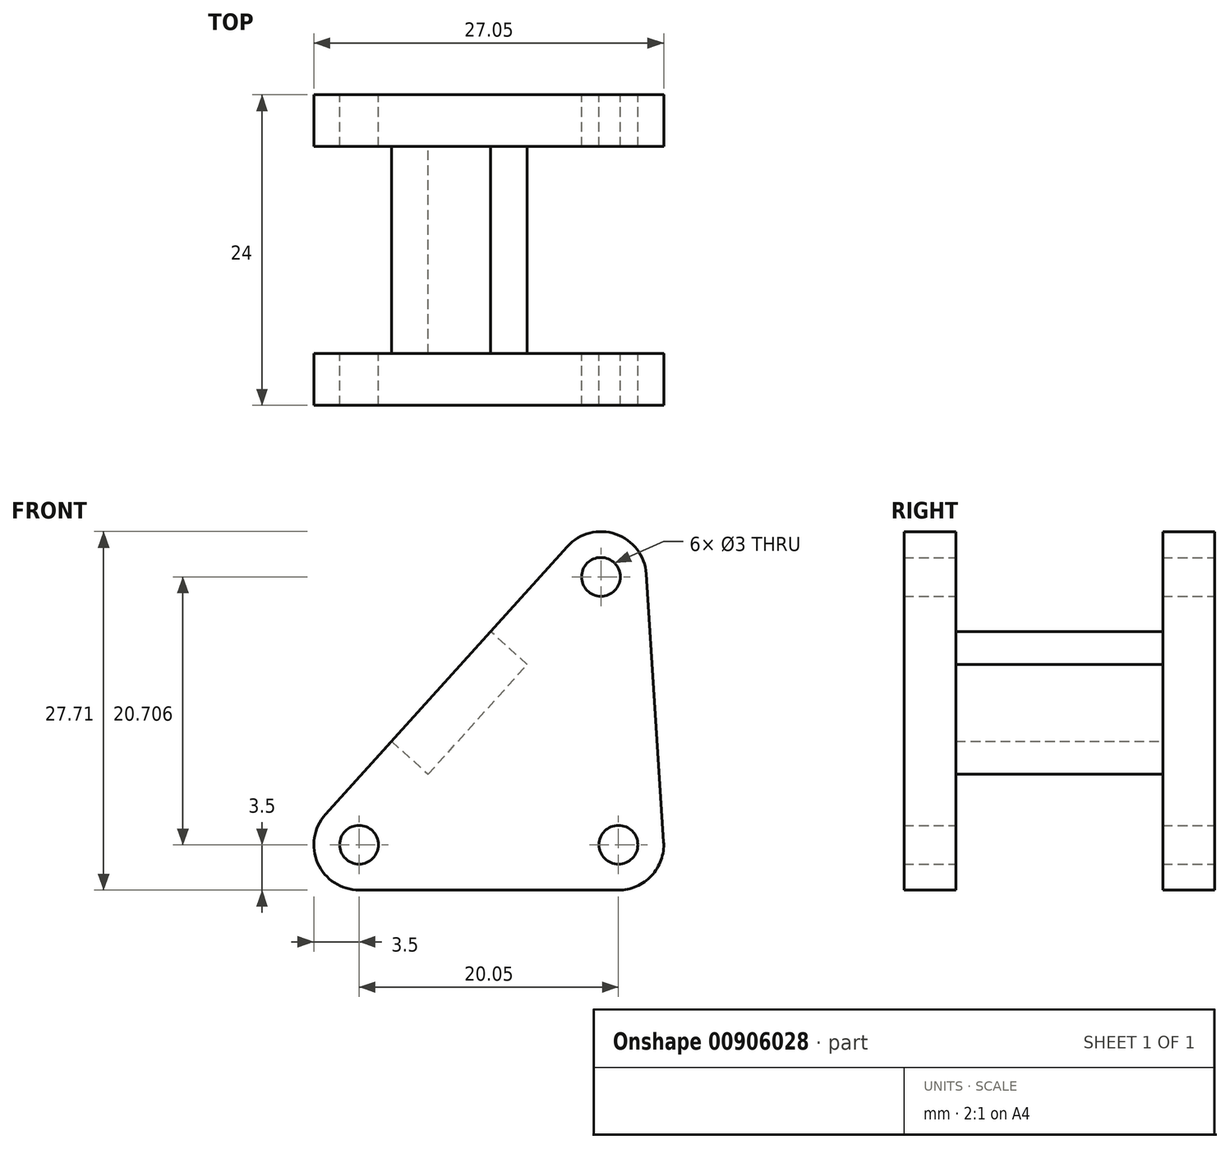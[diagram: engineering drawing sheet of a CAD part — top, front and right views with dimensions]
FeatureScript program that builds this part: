
annotation { "Feature Type Name" : "Feature", "Feature Type Description" : "" }
export const myFeature = defineFeature(function(context is Context, id is Id, definition is map)
    precondition{}
    {
        {
            var Q0;
            Q0=qCreatedBy(makeId("Front.planeOp"),FACE);
            var sketch = newSketch(context, id + "F0", { "sketchPlane" : qUnion([Q0])});
            skCircle(sketch, "E0", {"center": v(0, 0) * mm, "radius": 1.5 * mm});
            skCircle(sketch, "E1", {"center": v(20.05, 0) * mm, "radius": 1.5 * mm});
            skCircle(sketch, "E2", {"center": v(18.7, 20.7) * mm, "radius": 1.5 * mm});
            skLineSegment(sketch, "E3", {"start": v(-2.6, 2.35) * mm, "end": v(16.1, 23.05) * mm});
            skLineSegment(sketch, "E4", {"start": v(22.2, 20.93) * mm, "end": v(23.54, 0.23) * mm});
            skLineSegment(sketch, "E5", {"start": v(20.05, -3.5) * mm, "end": v(0, -3.5) * mm});
            skPoint(sketch, "E6.visualSharp", {"position": v(-7.88, -3.5) * mm});
            skArc(sketch, "E6.filletArc", {"start": v(-2.6, 2.35) * mm, "mid": v(-3.2, -1.42) * mm, "end": v(0, -3.5) * mm});
            skPoint(sketch, "E7.visualSharp", {"position": v(23.79, -3.5) * mm});
            skArc(sketch, "E7.filletArc", {"start": v(20.05, -3.5) * mm, "mid": v(22.6, -2.4) * mm, "end": v(23.54, 0.23) * mm});
            skPoint(sketch, "E8.visualSharp", {"position": v(21.65, 29.2) * mm});
            skArc(sketch, "E8.filletArc", {"start": v(22.2, 20.93) * mm, "mid": v(19.85, 24.01) * mm, "end": v(16.1, 23.05) * mm});
            skSolve(sketch);
        }
        {
            var Q0;
            Q0=qSketchRegion(id+"F0",true);
            extrude(context, id + "F1", {"entities" : qUnion([Q0]), "endBound" : BoundingType.SYMMETRIC, "depth" : 24 * mm, "offsetDistance" : 25.4 * mm});
        }
        {
            var Q0;
            Q0=qCreatedBy(makeId("Front.planeOp"),FACE);
            var sketch = newSketch(context, id + "F2", { "sketchPlane" : qUnion([Q0])});
            skLineSegment(sketch, "E9", {"start": v(2.5, 8) * mm, "end": v(5.34, 5.45) * mm});
            skLineSegment(sketch, "E10", {"start": v(5.34, 5.45) * mm, "end": v(13, 13.93) * mm});
            skLineSegment(sketch, "E11", {"start": v(13, 13.93) * mm, "end": v(10.17, 16.48) * mm});
            skLineSegment(sketch, "E12", {"start": v(10.17, 16.48) * mm, "end": v(2.5, 8) * mm});
            skSolve(sketch);
        }
        {
            var Q0;
            Q0=qCreatedBy(makeId("Front.planeOp"),FACE);
            var sketch = newSketch(context, id + "F3", { "sketchPlane" : qUnion([Q0])});
            skLineSegment(sketch, "E13.0.0", {"start": v(0, -3.5) * mm, "end": v(20.05, -3.5) * mm});
            skArc(sketch, "E13.0.1", {"start": v(20.05, -3.5) * mm, "mid": v(22.6, -2.4) * mm, "end": v(23.54, 0.23) * mm});
            skLineSegment(sketch, "E13.0.2", {"start": v(23.54, 0.23) * mm, "end": v(22.2, 20.93) * mm});
            skArc(sketch, "E13.0.3", {"start": v(22.2, 20.93) * mm, "mid": v(19.85, 24.01) * mm, "end": v(16.1, 23.05) * mm});
            skLineSegment(sketch, "E13.0.4", {"start": v(16.1, 23.05) * mm, "end": v(-2.6, 2.35) * mm});
            skArc(sketch, "E13.0.5", {"start": v(-2.6, 2.35) * mm, "mid": v(-3.2, -1.42) * mm, "end": v(0, -3.5) * mm});
            skSolve(sketch);
        }
        {
            var Q0;
            Q0=qSketchRegion(id+"F3",true);
            extrude(context, id + "F4", {"entities" : qUnion([Q0]), "operationType" : NewBodyOperationType.REMOVE, "endBound" : BoundingType.SYMMETRIC, "oppositeDirection" : true, "depth" : 16 * mm, "offsetDistance" : 25.4 * mm});
        }
        {
            var Q0;
            Q0=makeQuery(id+"F2.imprint","IMPRINT",FACE,{"disambiguationData":[TD([[makeQuery(id+"F2.imprint","IMPRINT",EDGE,{"derivedFrom":sQuery(id+"F2.wireOp",EDGE,"E9")}),1.0]])]});
            extrude(context, id + "F5", {"entities" : qUnion([Q0]), "endBound" : BoundingType.SYMMETRIC, "depth" : 16 * mm, "offsetDistance" : 25.4 * mm});
        }
    });
